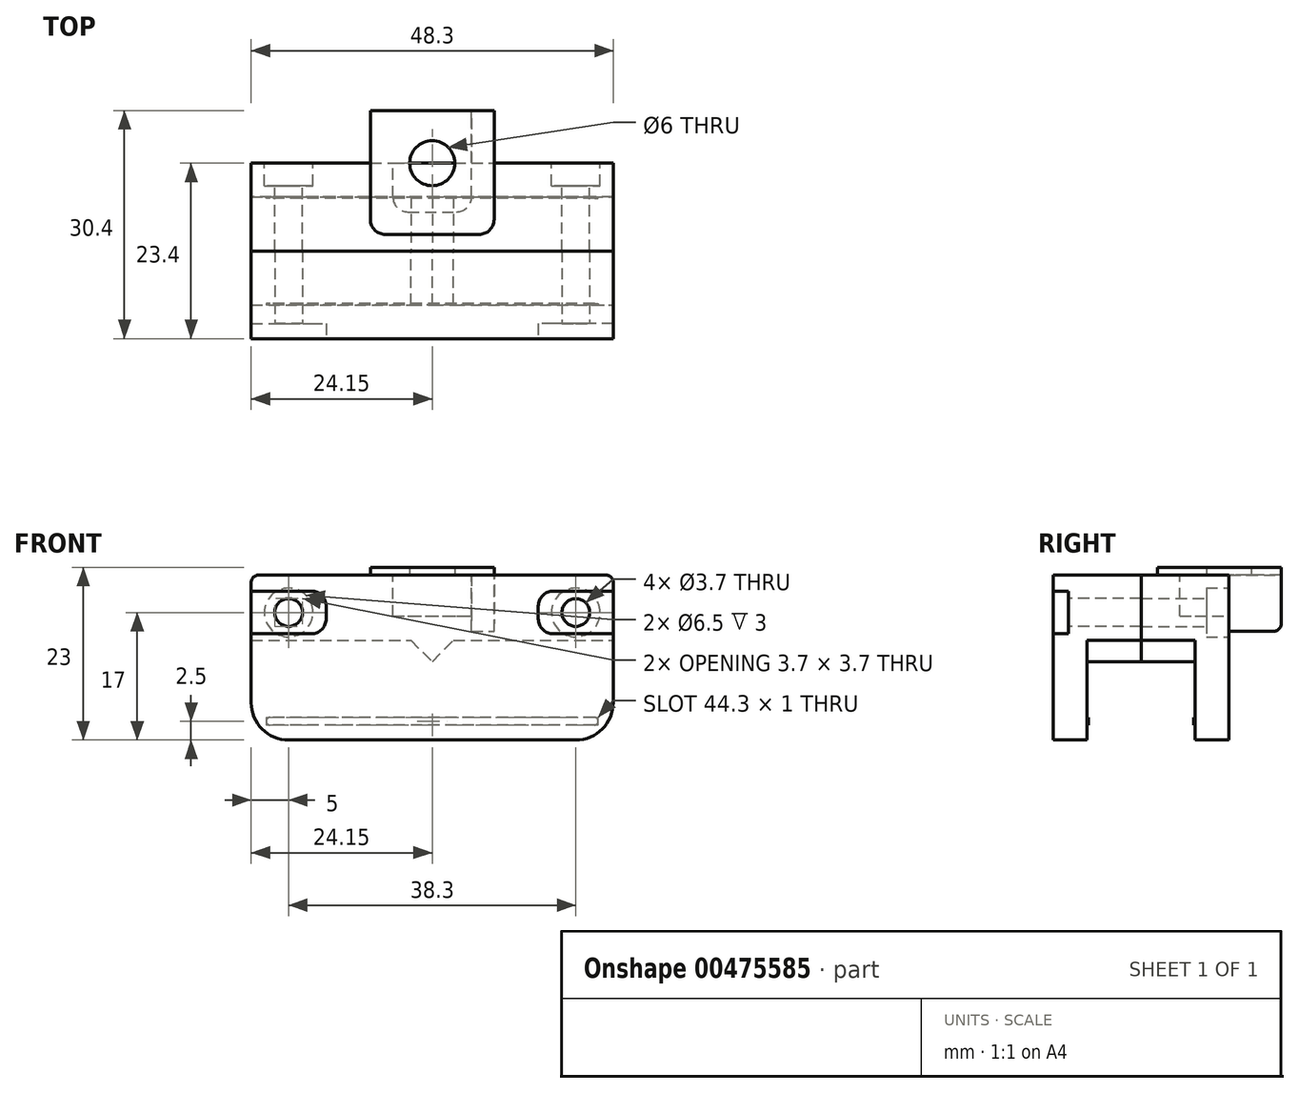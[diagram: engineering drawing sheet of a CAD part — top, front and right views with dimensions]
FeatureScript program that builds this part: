
annotation { "Feature Type Name" : "Feature", "Feature Type Description" : "" }
export const myFeature = defineFeature(function(context is Context, id is Id, definition is map)
    precondition{}
    {
        {
            var Q0;
            Q0=qCreatedBy(makeId("Front.planeOp"),FACE);
            var sketch = newSketch(context, id + "F0", { "sketchPlane" : qUnion([Q0])});
            skLineSegment(sketch, "E0", {"start": v(0, 0) * mm, "end": v(0, 42) * mm, "construction": true});
            skSolve(sketch);
        }
        {
            var Q0;
            Q0=qCreatedBy(makeId("Front.planeOp"),FACE);
            var sketch = newSketch(context, id + "F1", { "sketchPlane" : qUnion([Q0])});
            skLineSegment(sketch, "E1", {"start": v(-24.15, -8.7) * mm, "end": v(-2.85, -8.7) * mm});
            skLineSegment(sketch, "E2", {"start": v(-2.85, -8.7) * mm, "end": v(0, -11.55) * mm});
            skLineSegment(sketch, "E3", {"start": v(0, -11.55) * mm, "end": v(2.85, -8.7) * mm});
            skLineSegment(sketch, "E4", {"start": v(2.85, -8.7) * mm, "end": v(24.15, -8.7) * mm});
            skLineSegment(sketch, "E5", {"start": v(-24.15, -8.7) * mm, "end": v(-24.15, 0) * mm});
            skLineSegment(sketch, "E6", {"start": v(-24.15, 0) * mm, "end": v(24.15, 0) * mm});
            skLineSegment(sketch, "E7", {"start": v(24.15, -8.7) * mm, "end": v(24.15, 0) * mm});
            skSolve(sketch);
        }
        {
            var Q0;
            Q0=qSketchRegion(id+"F1",true);
            extrude(context, id + "F2", {"entities" : qUnion([Q0]), "oppositeDirection" : true, "depth" : 7.2 * mm});
        }
        {
            var Q0;
            Q0=makeQuery(id+"F2.opExtrude","CAP_FACE",FACE,{"disambiguationData":[OSD([sQuery(id+"F1.wireOp",EDGE,"E1"),sQuery(id+"F1.wireOp",EDGE,"E2"),sQuery(id+"F1.wireOp",EDGE,"E3"),sQuery(id+"F1.wireOp",EDGE,"E4"),sQuery(id+"F1.wireOp",EDGE,"E5"),sQuery(id+"F1.wireOp",EDGE,"E6"),sQuery(id+"F1.wireOp",EDGE,"E7")])],"isStart":false});
            var sketch = newSketch(context, id + "F3", { "sketchPlane" : qUnion([Q0])});
            skLineSegment(sketch, "E8.bottom", {"start": v(-24.15, 0) * mm, "end": v(24.15, 0) * mm});
            skLineSegment(sketch, "E8.top", {"start": v(-24.15, -22) * mm, "end": v(24.15, -22) * mm});
            skLineSegment(sketch, "E8.left", {"start": v(-24.15, 0) * mm, "end": v(-24.15, -22) * mm});
            skLineSegment(sketch, "E8.right", {"start": v(24.15, 0) * mm, "end": v(24.15, -22) * mm});
            skSolve(sketch);
        }
        {
            var Q0;
            Q0=qSketchRegion(id+"F3",true);
            extrude(context, id + "F4", {"entities" : qUnion([Q0]), "operationType" : NewBodyOperationType.ADD, "depth" : 4.5 * mm});
        }
        {
            var Q0;
            Q0=makeQuery(id+"F4.opExtrude","CAP_FACE",FACE,{"disambiguationData":[OSD([sQuery(id+"F3.wireOp",EDGE,"E8.bottom"),sQuery(id+"F3.wireOp",EDGE,"E8.top"),sQuery(id+"F3.wireOp",EDGE,"E8.left"),sQuery(id+"F3.wireOp",EDGE,"E8.right")])],"isStart":false});
            var sketch = newSketch(context, id + "F5", { "sketchPlane" : qUnion([Q0])});
            skPoint(sketch, "E9", {"position": v(-19.15, -5) * mm});
            skPoint(sketch, "E10.MirrorP", {"position": v(19.15, -5) * mm});
            skSolve(sketch);
        }
        {
            var Q0;
            Q0=makeQuery(id+"F4.opExtrude","CAP_FACE",FACE,{"disambiguationData":[OSD([sQuery(id+"F3.wireOp",EDGE,"E8.bottom"),sQuery(id+"F3.wireOp",EDGE,"E8.top"),sQuery(id+"F3.wireOp",EDGE,"E8.left"),sQuery(id+"F3.wireOp",EDGE,"E8.right")])],"isStart":true});
            var sketch = newSketch(context, id + "F6", { "sketchPlane" : qUnion([Q0])});
            skLineSegment(sketch, "E11.bottom", {"start": v(21.65, -19) * mm, "end": v(-21.65, -19) * mm});
            skLineSegment(sketch, "E11.top", {"start": v(21.65, -20) * mm, "end": v(-21.65, -20) * mm});
            skLineSegment(sketch, "E11.left", {"start": v(22.15, -19.5) * mm, "end": v(22.15, -19.5) * mm});
            skLineSegment(sketch, "E11.right", {"start": v(-22.15, -19.5) * mm, "end": v(-22.15, -19.5) * mm});
            skPoint(sketch, "E11.middle", {"position": v(0, -19.5) * mm});
            skPoint(sketch, "E12.visualSharp", {"position": v(22.15, -19) * mm});
            skArc(sketch, "E12.filletArc", {"start": v(22.15, -19.5) * mm, "mid": v(22, -19.15) * mm, "end": v(21.65, -19) * mm});
            skPoint(sketch, "E13.visualSharp", {"position": v(22.15, -20) * mm});
            skArc(sketch, "E13.filletArc", {"start": v(21.65, -20) * mm, "mid": v(22, -19.85) * mm, "end": v(22.15, -19.5) * mm});
            skPoint(sketch, "E14.visualSharp", {"position": v(-22.15, -19) * mm});
            skArc(sketch, "E14.filletArc", {"start": v(-21.65, -19) * mm, "mid": v(-22, -19.15) * mm, "end": v(-22.15, -19.5) * mm});
            skPoint(sketch, "E15.visualSharp", {"position": v(-22.15, -20) * mm});
            skArc(sketch, "E15.filletArc", {"start": v(-22.15, -19.5) * mm, "mid": v(-22, -19.85) * mm, "end": v(-21.65, -20) * mm});
            skSolve(sketch);
        }
        {
            var Q0;
            Q0=qSketchRegion(id+"F6",true);
            extrude(context, id + "F7", {"entities" : qUnion([Q0]), "operationType" : NewBodyOperationType.ADD, "depth" : .2 * mm});
        }
        {
            var Q0;
            Q0=makeQuery(id+"F2.opExtrude","SWEPT_BODY",BODY,{"disambiguationData":[OSD([sQuery(id+"F1.wireOp",EDGE,"E1"),sQuery(id+"F1.wireOp",EDGE,"E2"),sQuery(id+"F1.wireOp",EDGE,"E3"),sQuery(id+"F1.wireOp",EDGE,"E4"),sQuery(id+"F1.wireOp",EDGE,"E5"),sQuery(id+"F1.wireOp",EDGE,"E6"),sQuery(id+"F1.wireOp",EDGE,"E7")])]});
            var Q1;
            Q1=qCreatedBy(makeId("Front.planeOp"),FACE);
            mirror(context, id + "F8", {"entities" : qUnion([Q0]), "mirrorPlane" : qUnion([Q1])});
        }
        {
            var Q0;
            Q0=makeQuery(id+"F8.opPattern","COPY",FACE,{"derivedFrom":makeQuery(id+"F4.opExtrude","CAP_FACE",FACE,{"disambiguationData":[OSD([sQuery(id+"F3.wireOp",EDGE,"E8.bottom"),sQuery(id+"F3.wireOp",EDGE,"E8.top"),sQuery(id+"F3.wireOp",EDGE,"E8.left"),sQuery(id+"F3.wireOp",EDGE,"E8.right")])],"isStart":false}),"instanceName":"1"});
            var sketch = newSketch(context, id + "F9", { "sketchPlane" : qUnion([Q0])});
            skPoint(sketch, "E16", {"position": v(-19.15, -5) * mm});
            skPoint(sketch, "E17.MirrorP", {"position": v(19.15, -5) * mm});
            skSolve(sketch);
        }
        {
            var Q0;
            Q0=sQuery(id+"F5.wireOp",VERTEX,"E9");
            var Q1;
            Q1=sQuery(id+"F5.wireOp",VERTEX,"E10.MirrorP");
            var Q2;
            Q2=makeQuery(id+"F2.opExtrude","SWEPT_BODY",BODY,{"disambiguationData":[OSD([sQuery(id+"F1.wireOp",EDGE,"E1"),sQuery(id+"F1.wireOp",EDGE,"E2"),sQuery(id+"F1.wireOp",EDGE,"E3"),sQuery(id+"F1.wireOp",EDGE,"E4"),sQuery(id+"F1.wireOp",EDGE,"E5"),sQuery(id+"F1.wireOp",EDGE,"E6"),sQuery(id+"F1.wireOp",EDGE,"E7")])]});
            hole(context, id + "F10", {"style" : HoleStyle.C_BORE, "endStyle" : HoleEndStyle.THROUGH, "holeDiameter" : 3.7 * mm, "cBoreDiameter" : 6.5 * mm, "cBoreDepth" : 3 * mm, "isTappedThrough" : true, "tappedDepth" : 12 * mm, "tapClearance" : 3, "locations" : qUnion([Q0, Q1]), "scope" : qUnion([Q2])});
        }
        {
            var Q0;
            Q0=sQuery(id+"F9.wireOp",VERTEX,"E16");
            var Q1;
            Q1=sQuery(id+"F9.wireOp",VERTEX,"E17.MirrorP");
            var Q2;
            Q2=makeQuery(id+"F8.opPattern","COPY",BODY,{"derivedFrom":makeQuery(id+"F2.opExtrude","SWEPT_BODY",BODY,{"disambiguationData":[OSD([sQuery(id+"F1.wireOp",EDGE,"E1"),sQuery(id+"F1.wireOp",EDGE,"E2"),sQuery(id+"F1.wireOp",EDGE,"E3"),sQuery(id+"F1.wireOp",EDGE,"E4"),sQuery(id+"F1.wireOp",EDGE,"E5"),sQuery(id+"F1.wireOp",EDGE,"E6"),sQuery(id+"F1.wireOp",EDGE,"E7")])]}),"instanceName":"1"});
            hole(context, id + "F11", {"style" : HoleStyle.SIMPLE, "endStyle" : HoleEndStyle.THROUGH, "holeDiameter" : 3.7 * mm, "isTappedThrough" : true, "tappedDepth" : 12 * mm, "tapClearance" : 3, "locations" : qUnion([Q0, Q1]), "scope" : qUnion([Q2])});
        }
        {
            var Q0;
            Q0=makeQuery(id+"F8.opPattern","COPY",FACE,{"derivedFrom":makeQuery(id+"F4.opExtrude","CAP_FACE",FACE,{"disambiguationData":[OSD([sQuery(id+"F3.wireOp",EDGE,"E8.bottom"),sQuery(id+"F3.wireOp",EDGE,"E8.top"),sQuery(id+"F3.wireOp",EDGE,"E8.left"),sQuery(id+"F3.wireOp",EDGE,"E8.right")])],"isStart":false}),"instanceName":"1"});
            var sketch = newSketch(context, id + "F12", { "sketchPlane" : qUnion([Q0])});
            skLineSegment(sketch, "E18.bottom", {"start": v(-24.15, -2.15) * mm, "end": v(-16.15, -2.15) * mm});
            skLineSegment(sketch, "E18.top", {"start": v(-24.15, -7.85) * mm, "end": v(-16.15, -7.85) * mm});
            skLineSegment(sketch, "E18.left", {"start": v(-24.15, -2.15) * mm, "end": v(-24.15, -7.85) * mm});
            skLineSegment(sketch, "E18.right", {"start": v(-14.15, -4.15) * mm, "end": v(-14.15, -5.85) * mm});
            skPoint(sketch, "E18.middle", {"position": v(-19.15, -5) * mm});
            skPoint(sketch, "E19.visualSharp", {"position": v(-14.15, -2.15) * mm});
            skArc(sketch, "E19.filletArc", {"start": v(-14.15, -4.15) * mm, "mid": v(-14.74, -2.74) * mm, "end": v(-16.15, -2.15) * mm});
            skPoint(sketch, "E20.visualSharp", {"position": v(-14.15, -7.85) * mm});
            skArc(sketch, "E20.filletArc", {"start": v(-16.15, -7.85) * mm, "mid": v(-14.74, -7.26) * mm, "end": v(-14.15, -5.85) * mm});
            skLineSegment(sketch, "E21.MirrorCS", {"start": v(14.15, -4.15) * mm, "end": v(14.15, -5.85) * mm});
            skArc(sketch, "E22.MirrorCS", {"start": v(16.15, -7.85) * mm, "mid": v(14.74, -7.26) * mm, "end": v(14.15, -5.85) * mm});
            skArc(sketch, "E23.MirrorCS", {"start": v(14.15, -4.15) * mm, "mid": v(14.74, -2.74) * mm, "end": v(16.15, -2.15) * mm});
            skPoint(sketch, "E24.MirrorP", {"position": v(19.15, -5) * mm});
            skLineSegment(sketch, "E25.MirrorCS", {"start": v(24.15, -7.85) * mm, "end": v(16.15, -7.85) * mm});
            skLineSegment(sketch, "E26.MirrorCS", {"start": v(24.15, -2.15) * mm, "end": v(24.15, -7.85) * mm});
            skLineSegment(sketch, "E27.MirrorCS", {"start": v(24.15, -2.15) * mm, "end": v(16.15, -2.15) * mm});
            skPoint(sketch, "E28.MirrorP", {"position": v(14.15, -7.85) * mm});
            skPoint(sketch, "E29.MirrorP", {"position": v(14.15, -2.15) * mm});
            skSolve(sketch);
        }
        {
            var Q0;
            Q0=qSketchRegion(id+"F12",true);
            extrude(context, id + "F13", {"entities" : qUnion([Q0]), "operationType" : NewBodyOperationType.REMOVE, "oppositeDirection" : true, "depth" : 2 * mm});
        }
        {
            var Q0;
            Q0=makeQuery(id+"F4.boolean.opBoolean","MERGE",EDGE,{"derivedFrom":[makeQuery(id+"F2.opExtrude","SWEPT_EDGE",EDGE,{"disambiguationData":[OSD([sQuery(id+"F1.wireOp",EDGE,"E5"),sQuery(id+"F1.wireOp",EDGE,"E6")])]}),makeQuery(id+"F4.opExtrude","SWEPT_EDGE",EDGE,{"disambiguationData":[OSD([sQuery(id+"F3.wireOp",EDGE,"E8.bottom"),sQuery(id+"F3.wireOp",EDGE,"E8.right")])]})]});
            var Q1;
            Q1=makeQuery(id+"F8.opPattern","COPY",EDGE,{"derivedFrom":makeQuery(id+"F4.boolean.opBoolean","MERGE",EDGE,{"derivedFrom":[makeQuery(id+"F2.opExtrude","SWEPT_EDGE",EDGE,{"disambiguationData":[OSD([sQuery(id+"F1.wireOp",EDGE,"E5"),sQuery(id+"F1.wireOp",EDGE,"E6")])]}),makeQuery(id+"F4.opExtrude","SWEPT_EDGE",EDGE,{"disambiguationData":[OSD([sQuery(id+"F3.wireOp",EDGE,"E8.bottom"),sQuery(id+"F3.wireOp",EDGE,"E8.right")])]})]}),"instanceName":"1"});
            var Q2;
            Q2=makeQuery(id+"F8.opPattern","COPY",EDGE,{"derivedFrom":makeQuery(id+"F4.boolean.opBoolean","MERGE",EDGE,{"derivedFrom":[makeQuery(id+"F2.opExtrude","SWEPT_EDGE",EDGE,{"disambiguationData":[OSD([sQuery(id+"F1.wireOp",EDGE,"E6"),sQuery(id+"F1.wireOp",EDGE,"E7")])]}),makeQuery(id+"F4.opExtrude","SWEPT_EDGE",EDGE,{"disambiguationData":[OSD([sQuery(id+"F3.wireOp",EDGE,"E8.bottom"),sQuery(id+"F3.wireOp",EDGE,"E8.left")])]})]}),"instanceName":"1"});
            var Q3;
            Q3=makeQuery(id+"F4.boolean.opBoolean","MERGE",EDGE,{"derivedFrom":[makeQuery(id+"F2.opExtrude","SWEPT_EDGE",EDGE,{"disambiguationData":[OSD([sQuery(id+"F1.wireOp",EDGE,"E6"),sQuery(id+"F1.wireOp",EDGE,"E7")])]}),makeQuery(id+"F4.opExtrude","SWEPT_EDGE",EDGE,{"disambiguationData":[OSD([sQuery(id+"F3.wireOp",EDGE,"E8.bottom"),sQuery(id+"F3.wireOp",EDGE,"E8.left")])]})]});
            fillet(context, id + "F14", {"entities" : qUnion([Q0, Q1, Q2, Q3]), "radius" : 1 * mm, "tangentPropagation" : true, "allowEdgeOverflow" : false});
        }
        {
            var Q0;
            Q0=makeQuery(id+"F4.opExtrude","SWEPT_EDGE",EDGE,{"disambiguationData":[OSD([sQuery(id+"F3.wireOp",EDGE,"E8.top"),sQuery(id+"F3.wireOp",EDGE,"E8.left")])]});
            var Q1;
            Q1=makeQuery(id+"F8.opPattern","COPY",EDGE,{"derivedFrom":makeQuery(id+"F4.opExtrude","SWEPT_EDGE",EDGE,{"disambiguationData":[OSD([sQuery(id+"F3.wireOp",EDGE,"E8.top"),sQuery(id+"F3.wireOp",EDGE,"E8.left")])]}),"instanceName":"1"});
            var Q2;
            Q2=makeQuery(id+"F8.opPattern","COPY",EDGE,{"derivedFrom":makeQuery(id+"F4.opExtrude","SWEPT_EDGE",EDGE,{"disambiguationData":[OSD([sQuery(id+"F3.wireOp",EDGE,"E8.top"),sQuery(id+"F3.wireOp",EDGE,"E8.right")])]}),"instanceName":"1"});
            var Q3;
            Q3=makeQuery(id+"F4.opExtrude","SWEPT_EDGE",EDGE,{"disambiguationData":[OSD([sQuery(id+"F3.wireOp",EDGE,"E8.top"),sQuery(id+"F3.wireOp",EDGE,"E8.right")])]});
            fillet(context, id + "F15", {"entities" : qUnion([Q0, Q1, Q2, Q3]), "radius" : 5 * mm, "tangentPropagation" : true, "allowEdgeOverflow" : false});
        }
        {
            var Q0;
            Q0=makeQuery(id+"F4.boolean.opBoolean","MERGE",FACE,{"derivedFrom":[makeQuery(id+"F2.opExtrude","SWEPT_FACE",FACE,{"disambiguationData":[OSD([sQuery(id+"F1.wireOp",EDGE,"E6")])]}),makeQuery(id+"F4.opExtrude","SWEPT_FACE",FACE,{"disambiguationData":[OSD([sQuery(id+"F3.wireOp",EDGE,"E8.bottom")])]})]});
            var sketch = newSketch(context, id + "F16", { "sketchPlane" : qUnion([Q0])});
            skLineSegment(sketch, "E30.bottom", {"start": v(-3.25, 5.2) * mm, "end": v(3.25, 5.2) * mm});
            skLineSegment(sketch, "E30.top", {"start": v(-5.25, 11.7) * mm, "end": v(5.25, 11.7) * mm});
            skLineSegment(sketch, "E30.left", {"start": v(-5.25, 7.2) * mm, "end": v(-5.25, 11.7) * mm});
            skLineSegment(sketch, "E30.right", {"start": v(5.25, 7.2) * mm, "end": v(5.25, 11.7) * mm});
            skPoint(sketch, "E31.visualSharp", {"position": v(5.25, 5.2) * mm});
            skArc(sketch, "E31.filletArc", {"start": v(3.25, 5.2) * mm, "mid": v(4.66, 5.79) * mm, "end": v(5.25, 7.2) * mm});
            skPoint(sketch, "E32.visualSharp", {"position": v(-5.25, 5.2) * mm});
            skArc(sketch, "E32.filletArc", {"start": v(-5.25, 7.2) * mm, "mid": v(-4.66, 5.79) * mm, "end": v(-3.25, 5.2) * mm});
            skSolve(sketch);
        }
        {
            var Q0;
            Q0 = qSketchRegion(id + "F16", true);
            extrude(context, id + "F17", {"entities" : qUnion([Q0]), "operationType" : NewBodyOperationType.REMOVE, "oppositeDirection" : true, "depth" : 5.5 * mm});
        }
        {
            var Q0;
            Q0=makeQuery(id+"F4.boolean.opBoolean","MERGE",FACE,{"derivedFrom":[makeQuery(id+"F2.opExtrude","SWEPT_FACE",FACE,{"disambiguationData":[OSD([sQuery(id+"F1.wireOp",EDGE,"E6")])]}),makeQuery(id+"F4.opExtrude","SWEPT_FACE",FACE,{"disambiguationData":[OSD([sQuery(id+"F3.wireOp",EDGE,"E8.bottom")])]})]});
            var sketch = newSketch(context, id + "F18", { "sketchPlane" : qUnion([Q0])});
            skCircle(sketch, "E33", {"center": v(0, 11.7) * mm, "radius": 3 * mm});
            skLineSegment(sketch, "E34.bottom", {"start": v(-8.25, 18.7) * mm, "end": v(8.25, 18.7) * mm});
            skLineSegment(sketch, "E34.top", {"start": v(-6.25, 2.2) * mm, "end": v(6.25, 2.2) * mm});
            skLineSegment(sketch, "E34.left", {"start": v(-8.25, 18.7) * mm, "end": v(-8.25, 4.2) * mm});
            skLineSegment(sketch, "E34.right", {"start": v(8.25, 18.7) * mm, "end": v(8.25, 4.2) * mm});
            skPoint(sketch, "E35.visualSharp", {"position": v(-8.25, 2.2) * mm});
            skArc(sketch, "E35.filletArc", {"start": v(-8.25, 4.2) * mm, "mid": v(-7.66, 2.79) * mm, "end": v(-6.25, 2.2) * mm});
            skPoint(sketch, "E36.visualSharp", {"position": v(8.25, 2.2) * mm});
            skArc(sketch, "E36.filletArc", {"start": v(6.25, 2.2) * mm, "mid": v(7.66, 2.79) * mm, "end": v(8.25, 4.2) * mm});
            skSolve(sketch);
        }
        {
            var Q0;
            Q0 = qSketchRegion(id + "F18", true);
            extrude(context, id + "F19", {"entities" : qUnion([Q0]), "operationType" : NewBodyOperationType.ADD, "depth" : 1 * mm});
        }
        {
            var Q0;
            Q0=makeQuery(id+"F19.opExtrude","SWEPT_FACE",FACE,{"disambiguationData":[OSD([sQuery(id+"F18.wireOp",EDGE,"E34.right")])]});
            var sketch = newSketch(context, id + "F20", { "sketchPlane" : qUnion([Q0])});
            skLineSegment(sketch, "E37", {"start": v(18.7, 0) * mm, "end": v(18.7, -6.5) * mm});
            skLineSegment(sketch, "E38", {"start": v(17.7, -7.5) * mm, "end": v(11.7, -7.5) * mm});
            skLineSegment(sketch, "E39", {"start": v(11.7, -7.5) * mm, "end": v(11.7, 0) * mm});
            skLineSegment(sketch, "E40", {"start": v(11.7, 0) * mm, "end": v(18.7, 0) * mm});
            skPoint(sketch, "E41.visualSharp", {"position": v(18.7, -7.5) * mm});
            skArc(sketch, "E41.filletArc", {"start": v(17.7, -7.5) * mm, "mid": v(18.4, -7.2) * mm, "end": v(18.7, -6.5) * mm});
            skSolve(sketch);
        }
        {
            var Q0;
            Q0 = qSketchRegion(id + "F20", true);
            var Q1;
            Q1=makeQuery(id+"F17.opExtrude","SWEPT_FACE",FACE,{"disambiguationData":[OSD([sQuery(id+"F16.wireOp",EDGE,"b2ed90d9-d4aa-4ed6-a914-c6248d4714b0.0")])]});
            extrude(context, id + "F21", {"entities" : qUnion([Q0]), "operationType" : NewBodyOperationType.ADD, "oppositeDirection" : true, "endBoundEntityFace" : qUnion([Q1]), "depth" : 3 * mm});
        }
    });
